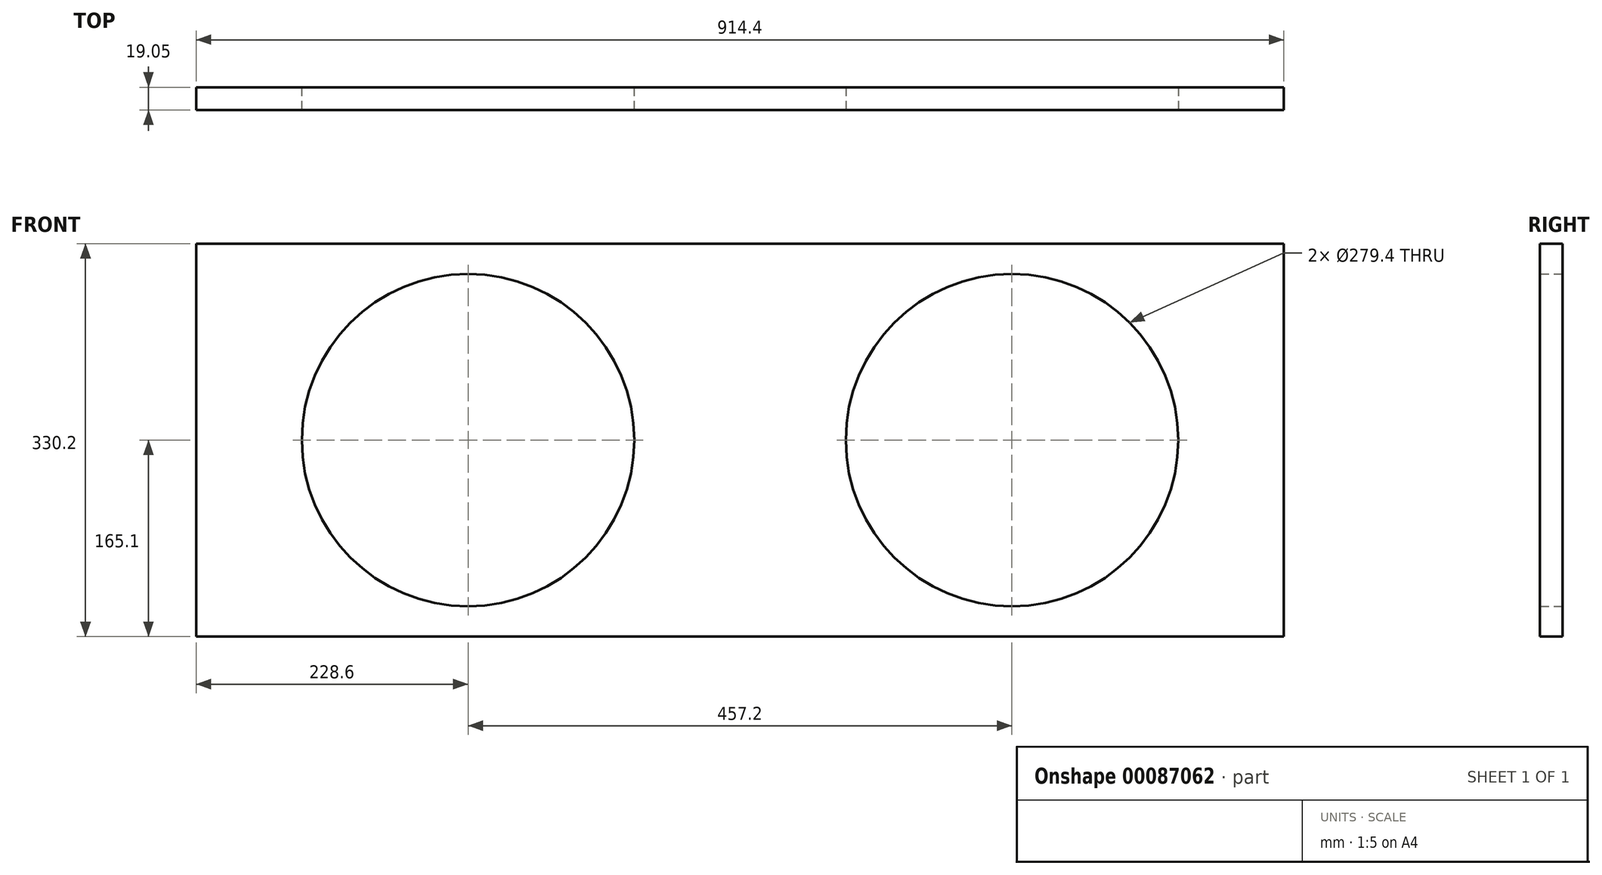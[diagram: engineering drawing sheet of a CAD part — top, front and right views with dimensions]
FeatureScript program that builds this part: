
annotation { "Feature Type Name" : "Feature", "Feature Type Description" : "" }
export const myFeature = defineFeature(function(context is Context, id is Id, definition is map)
    precondition{}
    {
        {
            var Q0;
            Q0=qCreatedBy(makeId("Front.planeOp"),FACE);
            var sketch = newSketch(context, id + "F0", { "sketchPlane" : qUnion([Q0])});
            skLineSegment(sketch, "E0.bottom", {"start": v(-457.2, 165.1) * mm, "end": v(457.2, 165.1) * mm});
            skLineSegment(sketch, "E0.top", {"start": v(-457.2, -165.1) * mm, "end": v(457.2, -165.1) * mm});
            skLineSegment(sketch, "E0.left", {"start": v(-457.2, 165.1) * mm, "end": v(-457.2, -165.1) * mm});
            skLineSegment(sketch, "E0.right", {"start": v(457.2, 165.1) * mm, "end": v(457.2, -165.1) * mm});
            skPoint(sketch, "E0.middle", {"position": v(0, 0) * mm});
            skSolve(sketch);
        }
        {
            var Q0;
            Q0=makeQuery(id+"F0.imprint","IMPRINT",FACE,{"disambiguationData":[TD([[makeQuery(id+"F0.imprint","IMPRINT",EDGE,{"derivedFrom":sQuery(id+"F0.wireOp",EDGE,"E0.bottom")}),-1.0]])]});
            var sketch = newSketch(context, id + "F1", { "sketchPlane" : qUnion([Q0])});
            skLineSegment(sketch, "E1", {"start": v(0, 0) * mm, "end": v(0, 177.8) * mm, "construction": true});
            skLineSegment(sketch, "E2", {"start": v(0, 177.8) * mm, "end": v(-457.2, 177.8) * mm, "construction": true});
            skLineSegment(sketch, "E3", {"start": v(-457.2, 177.8) * mm, "end": v(-457.2, -177.8) * mm, "construction": true});
            skLineSegment(sketch, "E4", {"start": v(-457.2, -177.8) * mm, "end": v(0, -177.8) * mm, "construction": true});
            skLineSegment(sketch, "E5", {"start": v(0, -177.8) * mm, "end": v(0, 0) * mm, "construction": true});
            skLineSegment(sketch, "E6", {"start": v(-457.2, 0) * mm, "end": v(0, 0) * mm, "construction": true});
            skCircle(sketch, "E7", {"center": v(-228.6, 0) * mm, "radius": 139.7 * mm});
            skSolve(sketch);
        }
        {
            var Q0;
            Q0=makeQuery(id+"F0.imprint","IMPRINT",FACE,{"disambiguationData":[TD([[makeQuery(id+"F0.imprint","IMPRINT",EDGE,{"derivedFrom":sQuery(id+"F0.wireOp",EDGE,"E0.bottom")}),-1.0]])]});
            extrude(context, id + "F2", {"entities" : qUnion([Q0]), "depth" : 19.05 * mm});
        }
        {
            var Q0;
            Q0 = qSketchRegion(id + "F1", true);
            extrude(context, id + "F3", {"entities" : qUnion([Q0]), "operationType" : NewBodyOperationType.REMOVE, "endBound" : BoundingType.THROUGH_ALL, "oppositeDirection" : true, "depth" : 25.4 * mm});
        }
        {
            var Q0;
            Q0=makeQuery(id+"F1.imprint","IMPRINT",FACE,{"disambiguationData":[TD([[makeQuery(id+"F1.imprint","IMPRINT",EDGE,{"derivedFrom":sQuery(id+"F1.wireOp",EDGE,"E7")}),1.0]])]});
            extrude(context, id + "F4", {"entities" : qUnion([Q0]), "operationType" : NewBodyOperationType.REMOVE, "endBound" : BoundingType.THROUGH_ALL, "depth" : 25.4 * mm});
        }
        {
            var Q0;
            Q0=makeQuery(id+"F2.opExtrude","CAP_FACE",FACE,{"disambiguationData":[OSD([sQuery(id+"F0.wireOp",EDGE,"E0.bottom"),sQuery(id+"F0.wireOp",EDGE,"E0.top"),sQuery(id+"F0.wireOp",EDGE,"E0.left"),sQuery(id+"F0.wireOp",EDGE,"E0.right")])],"isStart":false});
            var sketch = newSketch(context, id + "F5", { "sketchPlane" : qUnion([Q0])});
            skLineSegment(sketch, "E8", {"start": v(0, 0) * mm, "end": v(457.2, 0) * mm, "construction": true});
            skLineSegment(sketch, "E9", {"start": v(457.2, 0) * mm, "end": v(457.2, 165.1) * mm, "construction": true});
            skLineSegment(sketch, "E10", {"start": v(457.2, 165.1) * mm, "end": v(0, -165.1) * mm, "construction": true});
            skCircle(sketch, "E11", {"center": v(228.6, 0) * mm, "radius": 139.7 * mm});
            skSolve(sketch);
        }
        {
            var Q0;
            Q0 = qSketchRegion(id + "F5", true);
            extrude(context, id + "F6", {"entities" : qUnion([Q0]), "operationType" : NewBodyOperationType.REMOVE, "endBound" : BoundingType.THROUGH_ALL, "oppositeDirection" : true, "depth" : 25.4 * mm});
        }
    });
